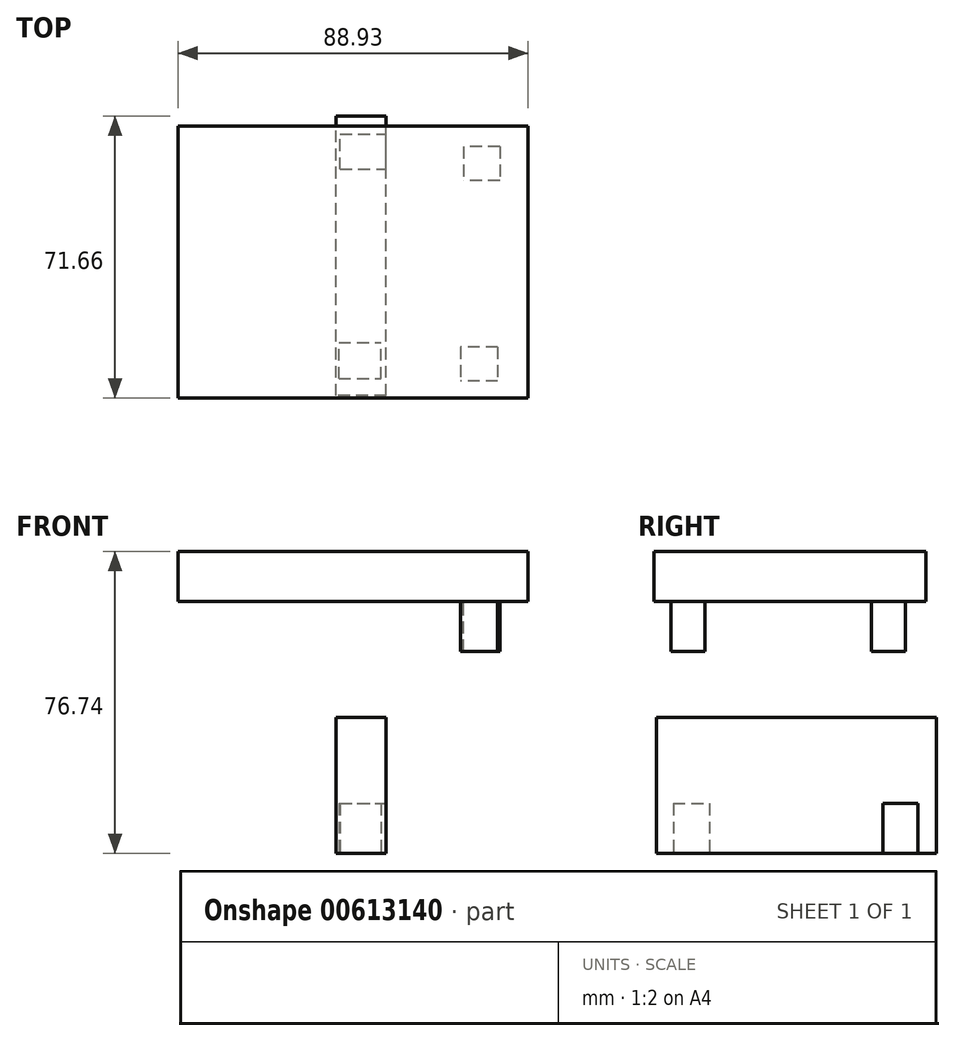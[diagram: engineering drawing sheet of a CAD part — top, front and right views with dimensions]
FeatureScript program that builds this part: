
annotation { "Feature Type Name" : "Feature", "Feature Type Description" : "" }
export const myFeature = defineFeature(function(context is Context, id is Id, definition is map)
    precondition{}
    {
        {
            var Q0;
            Q0=qCreatedBy(makeId("Top.planeOp"),FACE);
            var sketch = newSketch(context, id + "F0", { "sketchPlane" : qUnion([Q0])});
            skLineSegment(sketch, "E0.bottom", {"start": v(-40.15, 30.36) * mm, "end": v(48.78, 30.36) * mm});
            skLineSegment(sketch, "E0.top", {"start": v(-40.15, -38.7) * mm, "end": v(48.78, -38.7) * mm});
            skLineSegment(sketch, "E0.left", {"start": v(-40.15, 30.36) * mm, "end": v(-40.15, -38.7) * mm});
            skLineSegment(sketch, "E0.right", {"start": v(48.78, 30.36) * mm, "end": v(48.78, -38.7) * mm});
            skSolve(sketch);
        }
        {
            var Q0;
            Q0 = qSketchRegion(id + "F0", true);
            extrude(context, id + "F1", {"entities" : qUnion([Q0]), "depth" : 12.7 * mm, "offsetDistance" : 25.4 * mm});
        }
        {
            var Q0;
            Q0=makeQuery(id+"F1.opExtrude","CAP_FACE",FACE,{"disambiguationData":[OSD([sQuery(id+"F0.wireOp",EDGE,"E0.bottom"),sQuery(id+"F0.wireOp",EDGE,"E0.top"),sQuery(id+"F0.wireOp",EDGE,"E0.left"),sQuery(id+"F0.wireOp",EDGE,"E0.right")])],"isStart":true});
            var sketch = newSketch(context, id + "F2", { "sketchPlane" : qUnion([Q0])});
            skLineSegment(sketch, "E1.bottom", {"start": v(41.63, -25.18) * mm, "end": v(32.42, -25.18) * mm});
            skLineSegment(sketch, "E1.top", {"start": v(41.63, -16.55) * mm, "end": v(32.42, -16.55) * mm});
            skLineSegment(sketch, "E1.left", {"start": v(41.63, -25.18) * mm, "end": v(41.63, -16.55) * mm});
            skLineSegment(sketch, "E1.right", {"start": v(32.42, -25.18) * mm, "end": v(32.42, -16.55) * mm});
            skLineSegment(sketch, "E2.bottom", {"start": v(41.05, 25.76) * mm, "end": v(31.55, 25.76) * mm});
            skLineSegment(sketch, "E2.top", {"start": v(41.05, 34.4) * mm, "end": v(31.55, 34.4) * mm});
            skLineSegment(sketch, "E2.left", {"start": v(41.05, 25.76) * mm, "end": v(41.05, 34.4) * mm});
            skLineSegment(sketch, "E2.right", {"start": v(31.55, 25.76) * mm, "end": v(31.55, 34.4) * mm});
            skSolve(sketch);
        }
        {
            var Q0;
            Q0=makeQuery(id+"F2.imprint","IMPRINT",FACE,{"disambiguationData":[TD([[makeQuery(id+"F2.imprint","IMPRINT",EDGE,{"derivedFrom":sQuery(id+"F2.wireOp",EDGE,"E2.bottom")}),-1.0]])]});
            var Q1;
            Q1=makeQuery(id+"F2.imprint","IMPRINT",FACE,{"disambiguationData":[TD([[makeQuery(id+"F2.imprint","IMPRINT",EDGE,{"derivedFrom":sQuery(id+"F2.wireOp",EDGE,"E1.bottom")}),-1.0]])]});
            extrude(context, id + "F3", {"entities" : qUnion([Q0, Q1]), "operationType" : NewBodyOperationType.ADD, "depth" : 12.7 * mm, "offsetDistance" : 25.4 * mm});
        }
        {
            var Q0;
            Q0=qCreatedBy(makeId("Right.planeOp"),FACE);
            var sketch = newSketch(context, id + "F4", { "sketchPlane" : qUnion([Q0])});
            skLineSegment(sketch, "E3.bottom", {"start": v(-38.13, -29.5) * mm, "end": v(32.95, -29.5) * mm});
            skLineSegment(sketch, "E3.top", {"start": v(-38.13, -64.04) * mm, "end": v(32.95, -64.04) * mm});
            skLineSegment(sketch, "E3.left", {"start": v(-38.13, -29.5) * mm, "end": v(-38.13, -64.04) * mm});
            skLineSegment(sketch, "E3.right", {"start": v(32.95, -29.5) * mm, "end": v(32.95, -64.04) * mm});
            skSolve(sketch);
        }
        {
            var Q0;
            Q0 = qSketchRegion(id + "F4", true);
            extrude(context, id + "F5", {"entities" : qUnion([Q0]), "depth" : 12.7 * mm, "offsetDistance" : 25.4 * mm});
        }
        {
            var Q0;
            Q0=makeQuery(id+"F5.opExtrude","SWEPT_FACE",FACE,{"disambiguationData":[OSD([sQuery(id+"F4.wireOp",EDGE,"E3.top")])]});
            var sketch = newSketch(context, id + "F6", { "sketchPlane" : qUnion([Q0])});
            skLineSegment(sketch, "E4.bottom", {"start": v(0.72, 33.82) * mm, "end": v(11.38, 33.82) * mm});
            skLineSegment(sketch, "E4.top", {"start": v(0.72, 24.6) * mm, "end": v(11.38, 24.6) * mm});
            skLineSegment(sketch, "E4.left", {"start": v(0.72, 33.82) * mm, "end": v(0.72, 24.6) * mm});
            skLineSegment(sketch, "E4.right", {"start": v(11.38, 33.82) * mm, "end": v(11.38, 24.6) * mm});
            skLineSegment(sketch, "E5.bottom", {"start": v(1, -19.43) * mm, "end": v(12.7, -19.43) * mm});
            skLineSegment(sketch, "E5.top", {"start": v(1, -28.35) * mm, "end": v(12.7, -28.35) * mm});
            skLineSegment(sketch, "E5.left", {"start": v(1, -19.43) * mm, "end": v(1, -28.35) * mm});
            skLineSegment(sketch, "E5.right", {"start": v(12.7, -19.43) * mm, "end": v(12.7, -28.35) * mm});
            skSolve(sketch);
        }
        {
            var Q0;
            Q0=makeQuery(id+"F6.imprint","IMPRINT",FACE,{"disambiguationData":[TD([[makeQuery(id+"F6.imprint","IMPRINT",EDGE,{"derivedFrom":sQuery(id+"F6.wireOp",EDGE,"E4.bottom")}),-1.0]])]});
            var Q1;
            Q1=makeQuery(id+"F6.imprint","IMPRINT",FACE,{"disambiguationData":[TD([[makeQuery(id+"F6.imprint","IMPRINT",EDGE,{"derivedFrom":sQuery(id+"F6.wireOp",EDGE,"E5.bottom")}),-1.0]])]});
            extrude(context, id + "F7", {"entities" : qUnion([Q0, Q1]), "operationType" : NewBodyOperationType.REMOVE, "oppositeDirection" : true, "depth" : 12.7 * mm, "offsetDistance" : 25.4 * mm});
        }
    });
